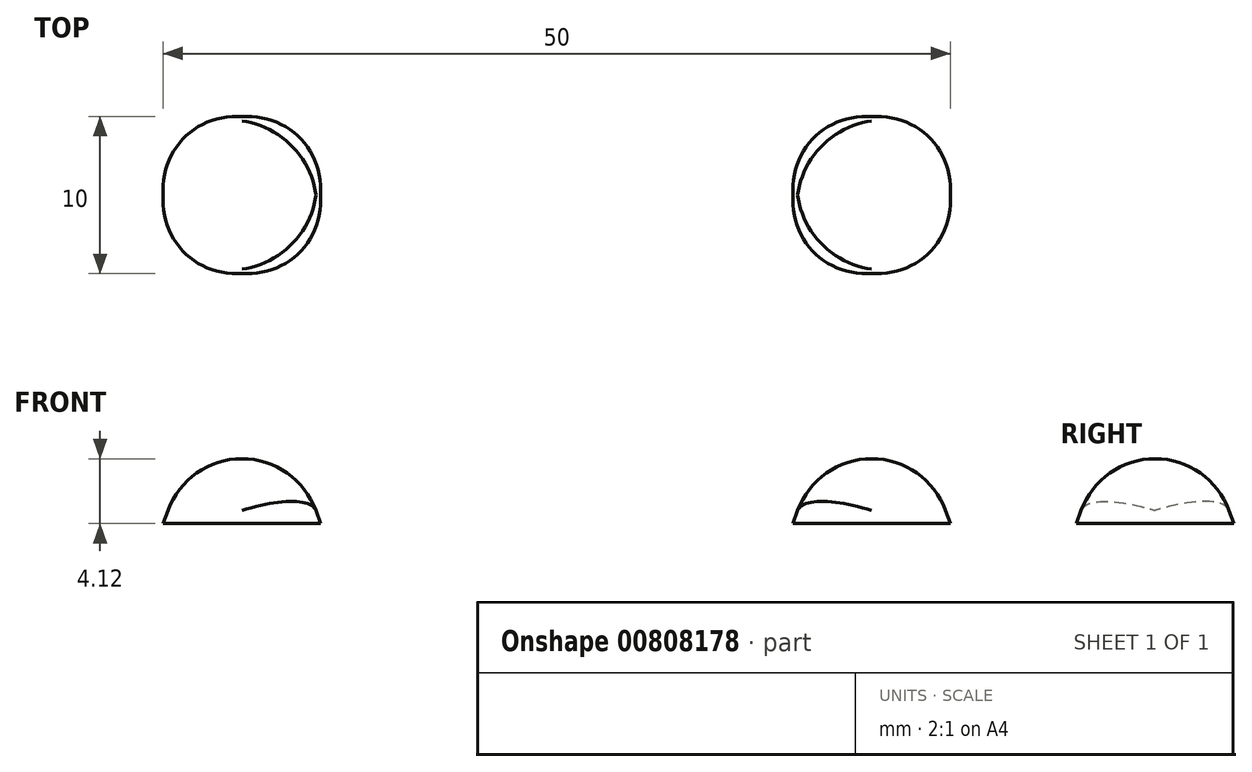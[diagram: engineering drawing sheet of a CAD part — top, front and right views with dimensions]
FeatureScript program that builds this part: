
annotation { "Feature Type Name" : "Feature", "Feature Type Description" : "" }
export const myFeature = defineFeature(function(context is Context, id is Id, definition is map)
    precondition{}
    {
        {
            var Q0;
            Q0=qCreatedBy(makeId("Top.planeOp"),FACE);
            var sketch = newSketch(context, id + "F0", { "sketchPlane" : qUnion([Q0])});
            skLineSegment(sketch, "E0.bottom", {"start": v(-25, 25) * mm, "end": v(25, 25) * mm});
            skLineSegment(sketch, "E0.top", {"start": v(-25, -25) * mm, "end": v(25, -25) * mm});
            skLineSegment(sketch, "E0.left", {"start": v(-25, 25) * mm, "end": v(-25, -25) * mm});
            skLineSegment(sketch, "E0.right", {"start": v(25, 25) * mm, "end": v(25, -25) * mm});
            skPoint(sketch, "E0.middle", {"position": v(0, 0) * mm});
            skLineSegment(sketch, "E1.bottom", {"start": v(-25, 25) * mm, "end": v(-15, 25) * mm});
            skLineSegment(sketch, "E1.top", {"start": v(-25, 15) * mm, "end": v(-15, 15) * mm});
            skLineSegment(sketch, "E1.left", {"start": v(-25, 25) * mm, "end": v(-25, 15) * mm});
            skLineSegment(sketch, "E1.right", {"start": v(-15, 25) * mm, "end": v(-15, 15) * mm});
            skLineSegment(sketch, "E2.bottom", {"start": v(-25, -25) * mm, "end": v(-15, -25) * mm});
            skLineSegment(sketch, "E2.top", {"start": v(-25, -15) * mm, "end": v(-15, -15) * mm});
            skLineSegment(sketch, "E2.left", {"start": v(-25, -25) * mm, "end": v(-25, -15) * mm});
            skLineSegment(sketch, "E2.right", {"start": v(-15, -25) * mm, "end": v(-15, -15) * mm});
            skLineSegment(sketch, "E3.bottom", {"start": v(25, -25) * mm, "end": v(15, -25) * mm});
            skLineSegment(sketch, "E3.top", {"start": v(25, -15) * mm, "end": v(15, -15) * mm});
            skLineSegment(sketch, "E3.left", {"start": v(25, -25) * mm, "end": v(25, -15) * mm});
            skLineSegment(sketch, "E3.right", {"start": v(15, -25) * mm, "end": v(15, -15) * mm});
            skLineSegment(sketch, "E4.bottom", {"start": v(25, 25) * mm, "end": v(15, 25) * mm});
            skLineSegment(sketch, "E4.top", {"start": v(25, 15) * mm, "end": v(15, 15) * mm});
            skLineSegment(sketch, "E4.left", {"start": v(25, 25) * mm, "end": v(25, 15) * mm});
            skLineSegment(sketch, "E4.right", {"start": v(15, 25) * mm, "end": v(15, 15) * mm});
            skPoint(sketch, "E5.visualSharp", {"position": v(-15, 15) * mm});
            skLineSegment(sketch, "E5.filletArc", {"start": v(-15, 15) * mm, "end": v(-15, 15) * mm});
            skPoint(sketch, "E6.visualSharp", {"position": v(-15, -15) * mm});
            skLineSegment(sketch, "E6.filletArc", {"start": v(-15, -15) * mm, "end": v(-15, -15) * mm});
            skPoint(sketch, "E7.visualSharp", {"position": v(15, -15) * mm});
            skLineSegment(sketch, "E7.filletArc", {"start": v(15, -15) * mm, "end": v(15, -15) * mm});
            skPoint(sketch, "E8.visualSharp", {"position": v(15, 15) * mm});
            skLineSegment(sketch, "E8.filletArc", {"start": v(15, 15) * mm, "end": v(15, 15) * mm});
            skSolve(sketch);
        }
        {
            var Q0;
            Q0=makeQuery(id+"F0.imprint","IMPRINT",FACE,{"disambiguationData":[TD([[makeQuery(id+"F0.imprint","IMPRINT",EDGE,{"derivedFrom":sQuery(id+"F0.wireOp",EDGE,"E0.bottom")}),-1.0]])]});
            extrude(context, id + "F1", {"entities" : qUnion([Q0]), "depth" : 40 * mm, "offsetDistance" : 25 * mm, "hasDraft" : true, "draftAngle" : 20 * degree, "draftPullDirection" : true});
        }
        {
            var Q0;
            Q0=makeQuery(id+"F1.opExtrude","SWEPT_EDGE",EDGE,{"disambiguationData":[OSD([sQuery(id+"F0.wireOp",EDGE,"E3.top"),sQuery(id+"F0.wireOp",EDGE,"E3.right")])]});
            var Q1;
            Q1=makeQuery(id+"F1.opExtrude","SWEPT_EDGE",EDGE,{"disambiguationData":[OSD([sQuery(id+"F0.wireOp",EDGE,"E2.top"),sQuery(id+"F0.wireOp",EDGE,"E2.right")])]});
            var Q2;
            Q2=makeQuery(id+"F1.opExtrude","SWEPT_EDGE",EDGE,{"disambiguationData":[OSD([sQuery(id+"F0.wireOp",EDGE,"E1.top"),sQuery(id+"F0.wireOp",EDGE,"E1.right")])]});
            var Q3;
            Q3=makeQuery(id+"F1.opExtrude","SWEPT_EDGE",EDGE,{"disambiguationData":[OSD([sQuery(id+"F0.wireOp",EDGE,"E4.top"),sQuery(id+"F0.wireOp",EDGE,"E4.right")])]});
            fillet(context, id + "F2", {"entities" : qUnion([Q0, Q1, Q2, Q3]), "radius" : 5 * mm, "tangentPropagation" : true, "allowEdgeOverflow" : false});
        }
        {
            var Q0;
            Q0=makeQuery(id+"F1.opExtrude","SWEPT_EDGE",EDGE,{"disambiguationData":[OSD([sQuery(id+"F0.wireOp",EDGE,"E0.left"),sQuery(id+"F0.wireOp",EDGE,"E2.top"),sQuery(id+"F0.wireOp",EDGE,"E2.left")])]});
            var Q1;
            Q1=makeQuery(id+"F1.opExtrude","SWEPT_EDGE",EDGE,{"disambiguationData":[OSD([sQuery(id+"F0.wireOp",EDGE,"E0.top"),sQuery(id+"F0.wireOp",EDGE,"E2.bottom"),sQuery(id+"F0.wireOp",EDGE,"E2.right")])]});
            var Q2;
            Q2=makeQuery(id+"F1.opExtrude","SWEPT_EDGE",EDGE,{"disambiguationData":[OSD([sQuery(id+"F0.wireOp",EDGE,"E0.top"),sQuery(id+"F0.wireOp",EDGE,"E3.bottom"),sQuery(id+"F0.wireOp",EDGE,"E3.right")])]});
            var Q3;
            Q3=makeQuery(id+"F1.opExtrude","SWEPT_EDGE",EDGE,{"disambiguationData":[OSD([sQuery(id+"F0.wireOp",EDGE,"E0.right"),sQuery(id+"F0.wireOp",EDGE,"E3.top"),sQuery(id+"F0.wireOp",EDGE,"E3.left")])]});
            var Q4;
            Q4=makeQuery(id+"F1.opExtrude","SWEPT_EDGE",EDGE,{"disambiguationData":[OSD([sQuery(id+"F0.wireOp",EDGE,"E0.right"),sQuery(id+"F0.wireOp",EDGE,"E4.top"),sQuery(id+"F0.wireOp",EDGE,"E4.left")])]});
            var Q5;
            Q5=makeQuery(id+"F1.opExtrude","SWEPT_EDGE",EDGE,{"disambiguationData":[OSD([sQuery(id+"F0.wireOp",EDGE,"E0.bottom"),sQuery(id+"F0.wireOp",EDGE,"E4.bottom"),sQuery(id+"F0.wireOp",EDGE,"E4.right")])]});
            var Q6;
            Q6=makeQuery(id+"F1.opExtrude","SWEPT_EDGE",EDGE,{"disambiguationData":[OSD([sQuery(id+"F0.wireOp",EDGE,"E0.bottom"),sQuery(id+"F0.wireOp",EDGE,"E1.bottom"),sQuery(id+"F0.wireOp",EDGE,"E1.right")])]});
            fillet(context, id + "F3", {"entities" : qUnion([Q0, Q1, Q2, Q3, Q4, Q5, Q6]), "radius" : 5 * mm, "tangentPropagation" : true, "allowEdgeOverflow" : false});
        }
    });
